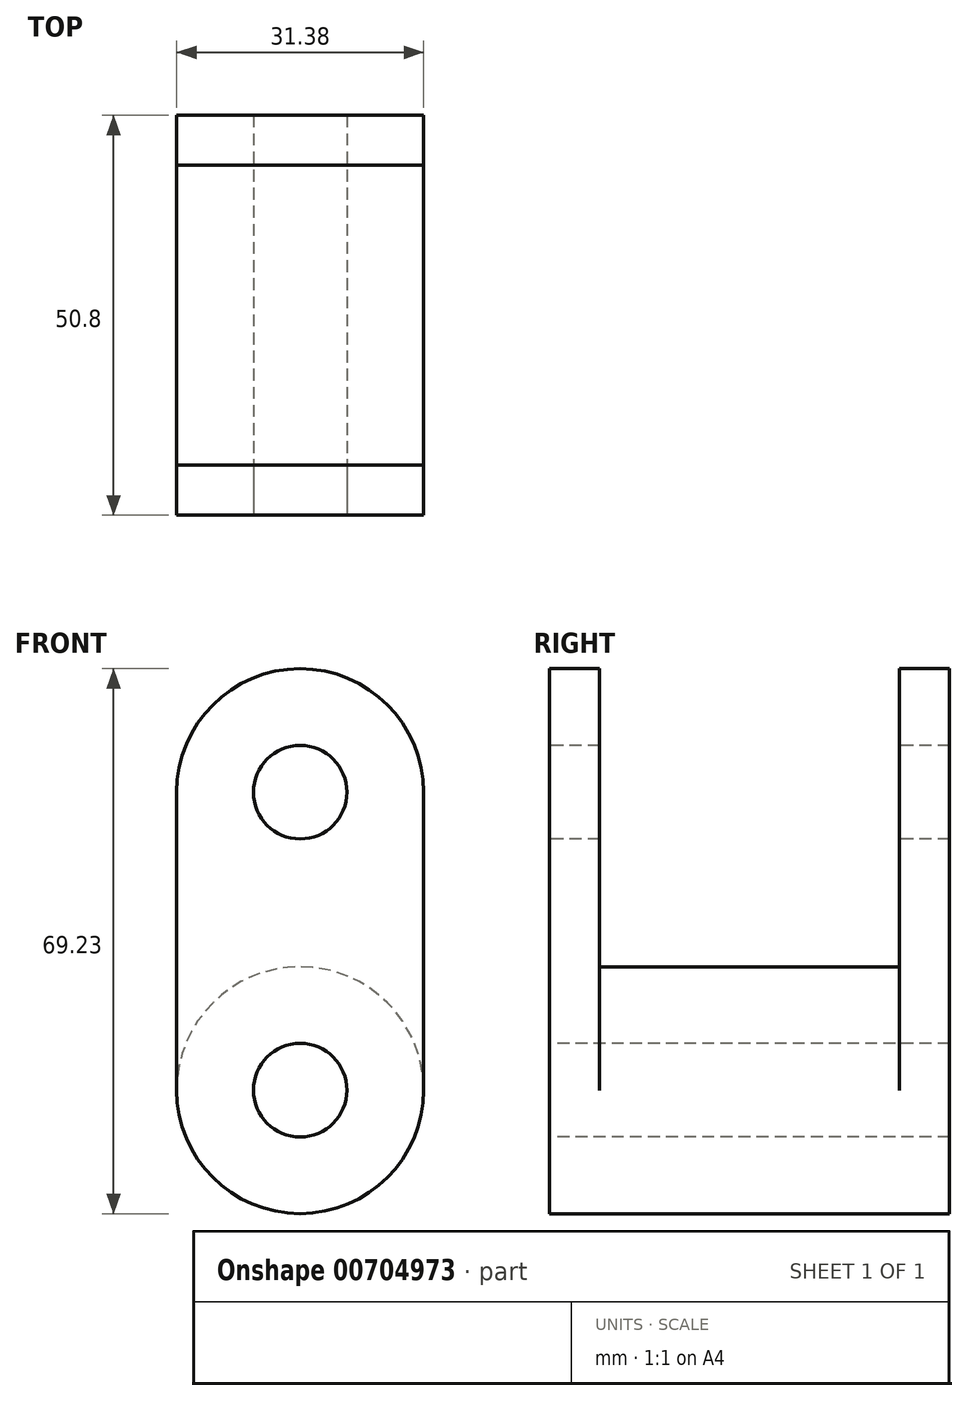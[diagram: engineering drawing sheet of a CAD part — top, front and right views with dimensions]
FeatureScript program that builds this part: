
annotation { "Feature Type Name" : "Feature", "Feature Type Description" : "" }
export const myFeature = defineFeature(function(context is Context, id is Id, definition is map)
    precondition{}
    {
        {
            var Q0;
            Q0=qCreatedBy(makeId("Front.planeOp"),FACE);
            var sketch = newSketch(context, id + "F0", { "sketchPlane" : qUnion([Q0])});
            skCircle(sketch, "E0", {"center": v(0, 0) * mm, "radius": 15.69 * mm});
            skSolve(sketch);
        }
        {
            var Q0;
            Q0 = qSketchRegion(id + "F0", true);
            extrude(context, id + "F1", {"entities" : qUnion([Q0]), "depth" : 25.4 * mm, "offsetDistance" : 25.4 * mm, "hasSecondDirection" : true, "secondDirectionOppositeDirection" : true, "secondDirectionDepth" : 25.4 * mm});
        }
        {
            var Q0;
            Q0=makeQuery(id+"F1.opExtrude","CAP_FACE",FACE,{"disambiguationData":[OSD([sQuery(id+"F0.wireOp",EDGE,"E0")])],"isStart":false});
            var sketch = newSketch(context, id + "F2", { "sketchPlane" : qUnion([Q0])});
            skArc(sketch, "E1.0", {"start": v(-15.69, 0) * mm, "mid": v(0, -15.69) * mm, "end": v(15.69, 0) * mm});
            skLineSegment(sketch, "E2", {"start": v(-15.69, 0) * mm, "end": v(-15.69, 37.85) * mm});
            skArc(sketch, "E3", {"start": v(0, 53.54) * mm, "mid": v(-11.1, 48.94) * mm, "end": v(-15.69, 37.85) * mm});
            skArc(sketch, "E4.MirrorCS", {"start": v(0, 53.54) * mm, "mid": v(11.1, 48.94) * mm, "end": v(15.69, 37.85) * mm});
            skLineSegment(sketch, "E5.MirrorCS", {"start": v(15.69, 0) * mm, "end": v(15.69, 37.85) * mm});
            skSolve(sketch);
        }
        {
            var Q0;
            Q0 = qSketchRegion(id + "F2", true);
            extrude(context, id + "F3", {"entities" : qUnion([Q0]), "operationType" : NewBodyOperationType.ADD, "oppositeDirection" : true, "depth" : 6.35 * mm, "offsetDistance" : 25.4 * mm});
        }
        {
            var Q0;
            Q0=makeQuery(id+"F1.opExtrude","SWEPT_BODY",BODY,{"disambiguationData":[OSD([sQuery(id+"F0.wireOp",EDGE,"E0")])]});
            var Q1;
            Q1=qCreatedBy(makeId("Front.planeOp"),FACE);
            mirror(context, id + "F4", {"operationType" : NewBodyOperationType.ADD, "entities" : qUnion([Q0]), "mirrorPlane" : qUnion([Q1])});
        }
        {
            var Q0;
            Q0=makeQuery(id+"F3.boolean.opBoolean","MERGE",FACE,{"derivedFrom":[makeQuery(id+"F1.opExtrude","CAP_FACE",FACE,{"disambiguationData":[OSD([sQuery(id+"F0.wireOp",EDGE,"E0")])],"isStart":false}),makeQuery(id+"F3.opExtrude","CAP_FACE",FACE,{"disambiguationData":[OSD([sQuery(id+"F2.wireOp",EDGE,"E1.0"),sQuery(id+"F2.wireOp",EDGE,"E2"),sQuery(id+"F2.wireOp",EDGE,"E3"),sQuery(id+"F2.wireOp",EDGE,"E4.MirrorCS"),sQuery(id+"F2.wireOp",EDGE,"E5.MirrorCS")])],"isStart":true})]});
            var sketch = newSketch(context, id + "F5", { "sketchPlane" : qUnion([Q0])});
            skCircle(sketch, "E6", {"center": v(0, 37.85) * mm, "radius": 5.94 * mm});
            skCircle(sketch, "E7", {"center": v(0, 0) * mm, "radius": 5.94 * mm});
            skSolve(sketch);
        }
        {
            var Q0;
            Q0 = qSketchRegion(id + "F5", true);
            extrude(context, id + "F6", {"entities" : qUnion([Q0]), "operationType" : NewBodyOperationType.REMOVE, "endBound" : BoundingType.THROUGH_ALL, "oppositeDirection" : true, "depth" : 25.4 * mm, "offsetDistance" : 25.4 * mm});
        }
    });
